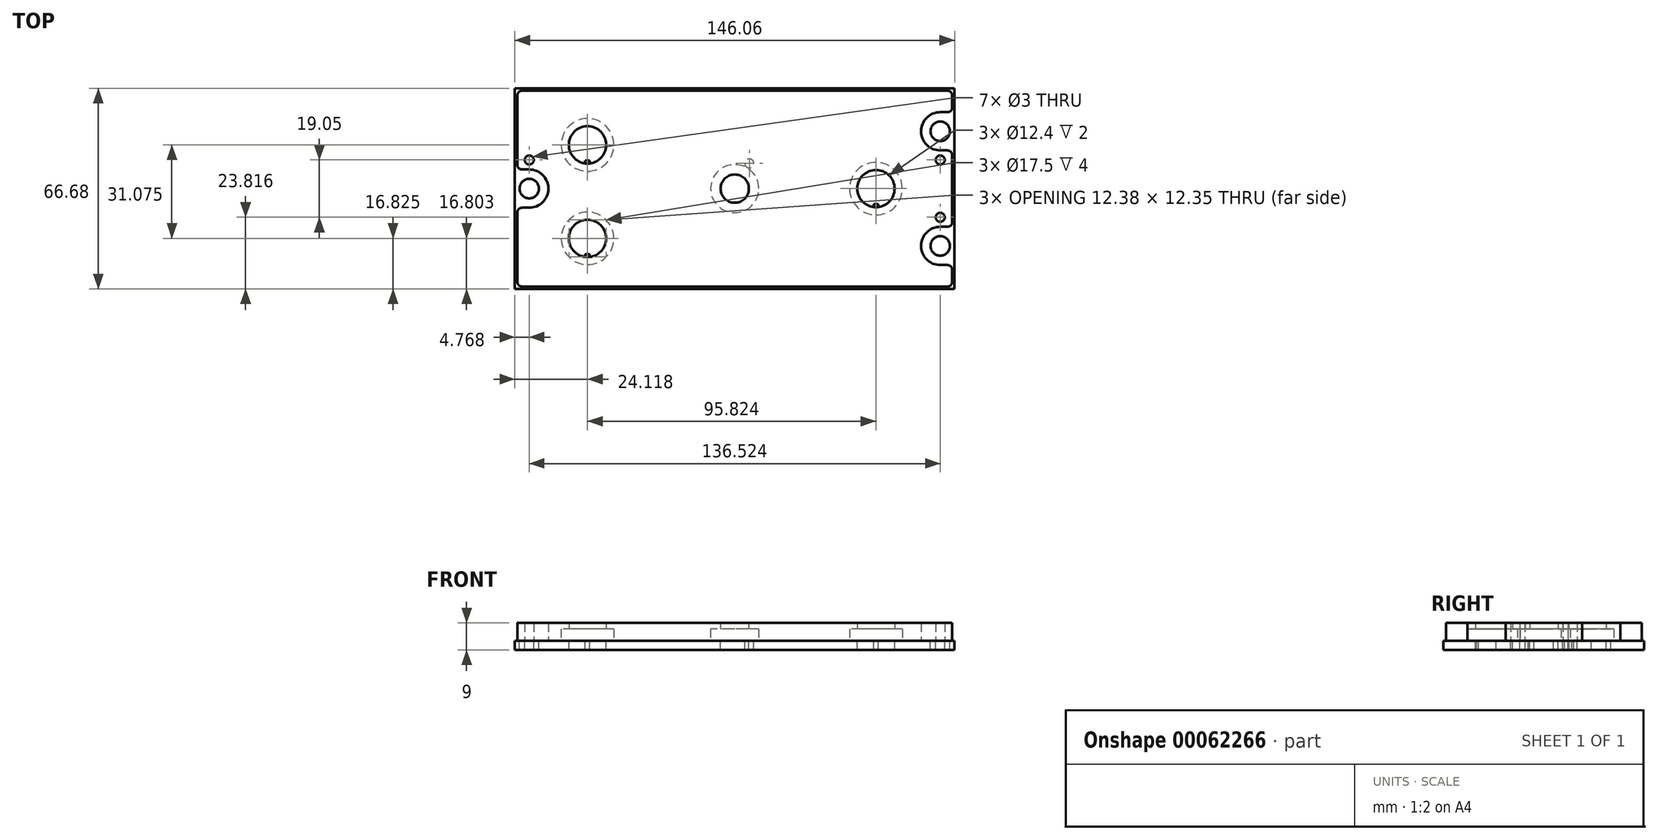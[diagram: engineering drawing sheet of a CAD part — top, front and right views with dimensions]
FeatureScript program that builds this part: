
annotation { "Feature Type Name" : "Feature", "Feature Type Description" : "" }
export const myFeature = defineFeature(function(context is Context, id is Id, definition is map)
    precondition{}
    {
        {
            var Q0;
            Q0=qCreatedBy(makeId("Top.planeOp"),FACE);
            var sketch = newSketch(context, id + "F0", { "sketchPlane" : qUnion([Q0])});
            skArc(sketch, "E0", {"start": v(68.26, -12.7) * mm, "mid": v(61.91, -19.05) * mm, "end": v(68.26, -25.4) * mm});
            skLineSegment(sketch, "E1", {"start": v(72.22, -32.54) * mm, "end": v(72.22, -25.4) * mm});
            skLineSegment(sketch, "E2", {"start": v(-72.23, -32.54) * mm, "end": v(-72.23, -25.4) * mm});
            skLineSegment(sketch, "E3", {"start": v(72.22, -32.54) * mm, "end": v(-72.23, -32.54) * mm});
            skArc(sketch, "E4", {"start": v(68.26, 25.4) * mm, "mid": v(61.91, 19.05) * mm, "end": v(68.26, 12.7) * mm});
            skLineSegment(sketch, "E5", {"start": v(-72.23, 32.54) * mm, "end": v(72.23, 32.54) * mm});
            skLineSegment(sketch, "E6", {"start": v(68.26, 12.7) * mm, "end": v(72.22, 12.7) * mm});
            skLineSegment(sketch, "E7", {"start": v(72.22, 25.4) * mm, "end": v(72.22, 32.54) * mm});
            skLineSegment(sketch, "E8", {"start": v(68.26, 25.4) * mm, "end": v(72.22, 25.4) * mm});
            skLineSegment(sketch, "E9", {"start": v(72.22, -12.7) * mm, "end": v(72.22, 12.7) * mm});
            skLineSegment(sketch, "E10", {"start": v(68.26, -12.7) * mm, "end": v(72.22, -12.7) * mm});
            skLineSegment(sketch, "E11", {"start": v(68.26, -25.4) * mm, "end": v(72.22, -25.4) * mm});
            skLineSegment(sketch, "E12", {"start": v(-72.23, -12.7) * mm, "end": v(-72.23, 12.7) * mm});
            skLineSegment(sketch, "E13", {"start": v(-72.23, 25.4) * mm, "end": v(-72.23, 32.54) * mm});
            skCircle(sketch, "E14", {"center": v(68.26, 19.05) * mm, "radius": 3.24 * mm});
            skCircle(sketch, "E15", {"center": v(68.26, -19.05) * mm, "radius": 3.24 * mm});
            skLineSegment(sketch, "E16", {"start": v(73.03, -33.34) * mm, "end": v(73.03, 33.34) * mm});
            skLineSegment(sketch, "E17", {"start": v(-73.03, 33.34) * mm, "end": v(73.03, 33.34) * mm});
            skLineSegment(sketch, "E18", {"start": v(-73.03, -33.34) * mm, "end": v(-73.03, 33.34) * mm});
            skLineSegment(sketch, "E19", {"start": v(73.03, -33.34) * mm, "end": v(-73.03, -33.34) * mm});
            skCircle(sketch, "E20", {"center": v(-68.26, 0) * mm, "radius": 3.24 * mm});
            skCircle(sketch, "E21", {"center": v(-68.26, 0) * mm, "radius": 6.35 * mm});
            skLineSegment(sketch, "E22", {"start": v(-68.26, 6.35) * mm, "end": v(-72.23, 6.35) * mm});
            skLineSegment(sketch, "E23.MirrorCS", {"start": v(-68.26, -6.35) * mm, "end": v(-72.23, -6.35) * mm});
            skCircle(sketch, "E24", {"center": v(-68.26, 9.53) * mm, "radius": 1.5 * mm});
            skCircle(sketch, "E25", {"center": v(68.26, 9.52) * mm, "radius": 1.5 * mm});
            skCircle(sketch, "E26", {"center": v(68.26, -9.52) * mm, "radius": 1.5 * mm});
            skLineSegment(sketch, "E27", {"start": v(-72.23, -25.4) * mm, "end": v(-72.23, -12.7) * mm});
            skLineSegment(sketch, "E28", {"start": v(-72.23, 25.4) * mm, "end": v(-72.23, 12.7) * mm});
            skPoint(sketch, "E29.endSnap0", {"position": v(-72.23, -19.05) * mm});
            skCircle(sketch, "E30", {"center": v(-48.91, -16.54) * mm, "radius": 6.2 * mm});
            skLineSegment(sketch, "E31.bottom", {"start": v(-48.16, -21.74) * mm, "end": v(-49.66, -21.74) * mm});
            skLineSegment(sketch, "E31.top", {"start": v(-48.16, -23.74) * mm, "end": v(-49.66, -23.74) * mm});
            skLineSegment(sketch, "E31.left", {"start": v(-48.16, -21.74) * mm, "end": v(-48.16, -23.74) * mm});
            skLineSegment(sketch, "E31.right", {"start": v(-49.66, -21.74) * mm, "end": v(-49.66, -23.74) * mm});
            skPoint(sketch, "E31.middle", {"position": v(-48.91, -22.74) * mm});
            skCircle(sketch, "E32.MirrorC", {"center": v(-48.91, 14.54) * mm, "radius": 6.2 * mm});
            skCircle(sketch, "E33", {"center": v(0, 0) * mm, "radius": 4.7 * mm});
            skCircle(sketch, "E34", {"center": v(0, 0) * mm, "radius": 8.7 * mm});
            skLineSegment(sketch, "E35", {"start": v(0, 0) * mm, "end": v(7.15, 12.39) * mm});
            skCircle(sketch, "E36", {"center": v(4.85, 8.4) * mm, "radius": 1.5 * mm});
            skLineSegment(sketch, "E37.bottom", {"start": v(-48.16, 9.34) * mm, "end": v(-49.66, 9.34) * mm});
            skLineSegment(sketch, "E37.top", {"start": v(-48.16, 7.34) * mm, "end": v(-49.66, 7.34) * mm});
            skLineSegment(sketch, "E37.left", {"start": v(-48.16, 9.34) * mm, "end": v(-48.16, 7.34) * mm});
            skLineSegment(sketch, "E37.right", {"start": v(-49.66, 9.34) * mm, "end": v(-49.66, 7.34) * mm});
            skPoint(sketch, "E37.middle", {"position": v(-48.91, 8.34) * mm});
            skCircle(sketch, "E38", {"center": v(46.91, 0) * mm, "radius": 6.2 * mm});
            skPoint(sketch, "E39.startSnap0", {"position": v(61.91, 19.05) * mm});
            skLineSegment(sketch, "E40.bottom", {"start": v(47.66, -5.2) * mm, "end": v(46.16, -5.2) * mm});
            skLineSegment(sketch, "E40.top", {"start": v(47.66, -7.2) * mm, "end": v(46.16, -7.2) * mm});
            skLineSegment(sketch, "E40.left", {"start": v(47.66, -5.2) * mm, "end": v(47.66, -7.2) * mm});
            skLineSegment(sketch, "E40.right", {"start": v(46.16, -5.2) * mm, "end": v(46.16, -7.2) * mm});
            skPoint(sketch, "E40.middle", {"position": v(46.91, -6.2) * mm});
            skSolve(sketch);
        }
        {
            var Q0;
            {var subQ0=sQuery(id+"F0.wireOp",EDGE,"E21");var subQ1=sQuery(id+"F0.wireOp",EDGE,"E12");var subQ2=makeQuery(id+"F0.imprint","INTERSECT",VERTEX,{"disambiguationData":[OD(0.0)],"derivedFrom":[subQ1,subQ0]});Q0=makeQuery(id+"F0.imprint","IMPRINT",FACE,{"disambiguationData":[TD([[makeQuery(id+"F0.imprint","IMPRINT",EDGE,{"disambiguationData":[TD([[subQ2,-1.0]])],"derivedFrom":subQ1}),1.0]])]});}
            var Q1;
            Q1=makeQuery(id+"F0.imprint","IMPRINT",FACE,{"disambiguationData":[TD([[makeQuery(id+"F0.imprint","IMPRINT",EDGE,{"derivedFrom":sQuery(id+"F0.wireOp",EDGE,"E10")}),-1.0]])]});
            var Q2;
            Q2=makeQuery(id+"F0.imprint","IMPRINT",FACE,{"disambiguationData":[TD([[makeQuery(id+"F0.imprint","IMPRINT",EDGE,{"derivedFrom":sQuery(id+"F0.wireOp",EDGE,"E10")}),1.0]])]});
            var Q3;
            {var subQ0=sQuery(id+"F0.wireOp",EDGE,"E22");Q3=makeQuery(id+"F0.imprint","IMPRINT",FACE,{"disambiguationData":[TD([[makeQuery(id+"F0.imprint","IMPRINT",EDGE,{"derivedFrom":subQ0}),1.0]])]});}
            var Q4;
            Q4=makeQuery(id+"F0.imprint","IMPRINT",FACE,{"disambiguationData":[TD([[makeQuery(id+"F0.imprint","IMPRINT",EDGE,{"derivedFrom":sQuery(id+"F0.wireOp",EDGE,"E20")}),-1.0]])]});
            var Q5;
            {var subQ0=sQuery(id+"F0.wireOp",EDGE,"E23.MirrorCS");Q5=makeQuery(id+"F0.imprint","IMPRINT",FACE,{"disambiguationData":[TD([[makeQuery(id+"F0.imprint","IMPRINT",EDGE,{"derivedFrom":subQ0}),-1.0]])]});}
            var Q6;
            {var subQ5=sQuery(id+"F0.wireOp",EDGE,"E31.bottom");Q6=makeQuery(id+"F0.imprint","IMPRINT",FACE,{"disambiguationData":[TD([[makeQuery(id+"F0.imprint","IMPRINT",EDGE,{"derivedFrom":subQ5}),1.0]])]});}
            var Q7;
            {var subQ5=sQuery(id+"F0.wireOp",EDGE,"E31.top");Q7=makeQuery(id+"F0.imprint","IMPRINT",FACE,{"disambiguationData":[TD([[makeQuery(id+"F0.imprint","IMPRINT",EDGE,{"derivedFrom":subQ5}),-1.0]])]});}
            var Q8;
            {var subQ5=sQuery(id+"F0.wireOp",EDGE,"E37.bottom");Q8=makeQuery(id+"F0.imprint","IMPRINT",FACE,{"disambiguationData":[TD([[makeQuery(id+"F0.imprint","IMPRINT",EDGE,{"derivedFrom":subQ5}),1.0]])]});}
            var Q9;
            {var subQ5=sQuery(id+"F0.wireOp",EDGE,"E37.top");Q9=makeQuery(id+"F0.imprint","IMPRINT",FACE,{"disambiguationData":[TD([[makeQuery(id+"F0.imprint","IMPRINT",EDGE,{"derivedFrom":subQ5}),-1.0]])]});}
            var Q10;
            Q10=makeQuery(id+"F0.imprint","IMPRINT",FACE,{"disambiguationData":[TD([[makeQuery(id+"F0.imprint","IMPRINT",EDGE,{"derivedFrom":sQuery(id+"F0.wireOp",EDGE,"E33")}),-1.0]])]});
            var Q11;
            {var subQ5=sQuery(id+"F0.wireOp",EDGE,"E40.bottom");Q11=makeQuery(id+"F0.imprint","IMPRINT",FACE,{"disambiguationData":[TD([[makeQuery(id+"F0.imprint","IMPRINT",EDGE,{"derivedFrom":subQ5}),1.0]])]});}
            var Q12;
            {var subQ5=sQuery(id+"F0.wireOp",EDGE,"E40.top");Q12=makeQuery(id+"F0.imprint","IMPRINT",FACE,{"disambiguationData":[TD([[makeQuery(id+"F0.imprint","IMPRINT",EDGE,{"derivedFrom":subQ5}),-1.0]])]});}
            extrude(context, id + "F1", {"entities" : qUnion([Q0, Q1, Q2, Q3, Q4, Q5, Q6, Q7, Q8, Q9, Q10, Q11, Q12]), "oppositeDirection" : true, "depth" : 3 * mm});
        }
        {
            var Q0;
            Q0=makeQuery(id+"F0.imprint","IMPRINT",FACE,{"disambiguationData":[TD([[makeQuery(id+"F0.imprint","IMPRINT",EDGE,{"derivedFrom":sQuery(id+"F0.wireOp",EDGE,"E10")}),1.0]])]});
            var Q1;
            {var subQ0=sQuery(id+"F0.wireOp",EDGE,"E35");var subQ1=sQuery(id+"F0.wireOp",EDGE,"E34");var subQ2=makeQuery(id+"F0.imprint","INTERSECT",VERTEX,{"derivedFrom":[subQ1,subQ0]});Q1=makeQuery(id+"F0.imprint","IMPRINT",FACE,{"disambiguationData":[TD([[makeQuery(id+"F0.imprint","IMPRINT",EDGE,{"disambiguationData":[TD([[subQ2,-1.0]])],"derivedFrom":subQ1}),-1.0]])]});}
            var Q2;
            {var subQ0=sQuery(id+"F0.wireOp",EDGE,"E35");var subQ1=sQuery(id+"F0.wireOp",EDGE,"E34");var subQ2=makeQuery(id+"F0.imprint","INTERSECT",VERTEX,{"derivedFrom":[subQ1,subQ0]});Q2=makeQuery(id+"F0.imprint","IMPRINT",FACE,{"disambiguationData":[TD([[makeQuery(id+"F0.imprint","IMPRINT",EDGE,{"disambiguationData":[TD([[subQ2,1.0]])],"derivedFrom":subQ1}),-1.0]])]});}
            var Q3;
            {var subQ0=sQuery(id+"F0.wireOp",EDGE,"E35");var subQ1=sQuery(id+"F0.wireOp",EDGE,"E34");var subQ2=makeQuery(id+"F0.imprint","INTERSECT",VERTEX,{"derivedFrom":[subQ1,subQ0]});Q3=makeQuery(id+"F0.imprint","IMPRINT",FACE,{"disambiguationData":[TD([[makeQuery(id+"F0.imprint","IMPRINT",EDGE,{"disambiguationData":[TD([[subQ2,1.0]])],"derivedFrom":subQ1}),1.0]])]});}
            var Q4;
            {var subQ0=sQuery(id+"F0.wireOp",EDGE,"E35");var subQ1=sQuery(id+"F0.wireOp",EDGE,"E34");var subQ2=makeQuery(id+"F0.imprint","INTERSECT",VERTEX,{"derivedFrom":[subQ1,subQ0]});Q4=makeQuery(id+"F0.imprint","IMPRINT",FACE,{"disambiguationData":[TD([[makeQuery(id+"F0.imprint","IMPRINT",EDGE,{"disambiguationData":[TD([[subQ2,-1.0]])],"derivedFrom":subQ1}),1.0]])]});}
            var Q5;
            Q5=makeQuery(id+"F0.imprint","IMPRINT",FACE,{"disambiguationData":[TD([[makeQuery(id+"F0.imprint","IMPRINT",EDGE,{"derivedFrom":sQuery(id+"F0.wireOp",EDGE,"E33")}),-1.0]])]});
            var Q6;
            {var subQ5=sQuery(id+"F0.wireOp",EDGE,"E31.top");Q6=makeQuery(id+"F0.imprint","IMPRINT",FACE,{"disambiguationData":[TD([[makeQuery(id+"F0.imprint","IMPRINT",EDGE,{"derivedFrom":subQ5}),-1.0]])]});}
            var Q7;
            {var subQ5=sQuery(id+"F0.wireOp",EDGE,"E37.top");Q7=makeQuery(id+"F0.imprint","IMPRINT",FACE,{"disambiguationData":[TD([[makeQuery(id+"F0.imprint","IMPRINT",EDGE,{"derivedFrom":subQ5}),-1.0]])]});}
            var Q8;
            {var subQ5=sQuery(id+"F0.wireOp",EDGE,"E40.top");Q8=makeQuery(id+"F0.imprint","IMPRINT",FACE,{"disambiguationData":[TD([[makeQuery(id+"F0.imprint","IMPRINT",EDGE,{"derivedFrom":subQ5}),-1.0]])]});}
            extrude(context, id + "F2", {"entities" : qUnion([Q0, Q1, Q2, Q3, Q4, Q5, Q6, Q7, Q8]), "depth" : 6 * mm});
        }
        {
            var Q0;
            Q0=makeQuery(id+"F0.imprint","IMPRINT",FACE,{"disambiguationData":[TD([[makeQuery(id+"F0.imprint","IMPRINT",EDGE,{"derivedFrom":sQuery(id+"F0.wireOp",EDGE,"E10")}),1.0]])]});
            var sketch = newSketch(context, id + "F3", { "sketchPlane" : qUnion([Q0])});
            skCircle(sketch, "E41", {"center": v(-48.91, 14.54) * mm, "radius": 8.75 * mm});
            skCircle(sketch, "E42", {"center": v(-48.91, -16.54) * mm, "radius": 8.75 * mm});
            skCircle(sketch, "E43", {"center": v(0, 0) * mm, "radius": 8 * mm});
            skCircle(sketch, "E44", {"center": v(46.91, 0) * mm, "radius": 8.75 * mm});
            skSolve(sketch);
        }
        {
            var Q0;
            Q0 = qSketchRegion(id + "F3", true);
            extrude(context, id + "F4", {"entities" : qUnion([Q0]), "operationType" : NewBodyOperationType.REMOVE, "depth" : 4 * mm});
        }
        {
            var Q0;
            Q0=makeQuery(id+"F2.opExtrude","SWEPT_EDGE",EDGE,{"disambiguationData":[OSD([sQuery(id+"F0.wireOp",EDGE,"E2"),sQuery(id+"F0.wireOp",EDGE,"E3")])]});
            var Q1;
            Q1=makeQuery(id+"F2.opExtrude","SWEPT_EDGE",EDGE,{"disambiguationData":[OSD([sQuery(id+"F0.wireOp",EDGE,"E12"),sQuery(id+"F0.wireOp",EDGE,"E23.MirrorCS")])]});
            var Q2;
            Q2=makeQuery(id+"F2.opExtrude","SWEPT_EDGE",EDGE,{"disambiguationData":[OSD([sQuery(id+"F0.wireOp",EDGE,"E12"),sQuery(id+"F0.wireOp",EDGE,"E22")])]});
            var Q3;
            Q3=makeQuery(id+"F2.opExtrude","SWEPT_EDGE",EDGE,{"disambiguationData":[OSD([sQuery(id+"F0.wireOp",EDGE,"E13"),sQuery(id+"F0.wireOp",EDGE,"E5")])]});
            var Q4;
            Q4=makeQuery(id+"F2.opExtrude","SWEPT_EDGE",EDGE,{"disambiguationData":[OSD([sQuery(id+"F0.wireOp",EDGE,"E1"),sQuery(id+"F0.wireOp",EDGE,"E3")])]});
            var Q5;
            Q5=makeQuery(id+"F2.opExtrude","SWEPT_EDGE",EDGE,{"disambiguationData":[OSD([sQuery(id+"F0.wireOp",EDGE,"E1"),sQuery(id+"F0.wireOp",EDGE,"E11")])]});
            var Q6;
            Q6=makeQuery(id+"F2.opExtrude","SWEPT_EDGE",EDGE,{"disambiguationData":[OSD([sQuery(id+"F0.wireOp",EDGE,"E10"),sQuery(id+"F0.wireOp",EDGE,"E9")])]});
            var Q7;
            Q7=makeQuery(id+"F2.opExtrude","SWEPT_EDGE",EDGE,{"disambiguationData":[OSD([sQuery(id+"F0.wireOp",EDGE,"E6"),sQuery(id+"F0.wireOp",EDGE,"E9")])]});
            var Q8;
            Q8=makeQuery(id+"F2.opExtrude","SWEPT_EDGE",EDGE,{"disambiguationData":[OSD([sQuery(id+"F0.wireOp",EDGE,"E8"),sQuery(id+"F0.wireOp",EDGE,"E7")])]});
            var Q9;
            Q9=makeQuery(id+"F2.opExtrude","SWEPT_EDGE",EDGE,{"disambiguationData":[OSD([sQuery(id+"F0.wireOp",EDGE,"E5"),sQuery(id+"F0.wireOp",EDGE,"E7")])]});
            fillet(context, id + "F5", {"entities" : qUnion([Q0, Q1, Q2, Q3, Q4, Q5, Q6, Q7, Q8, Q9]), "radius" : 1.59 * mm, "tangentPropagation" : true, "allowEdgeOverflow" : false});
        }
    });
